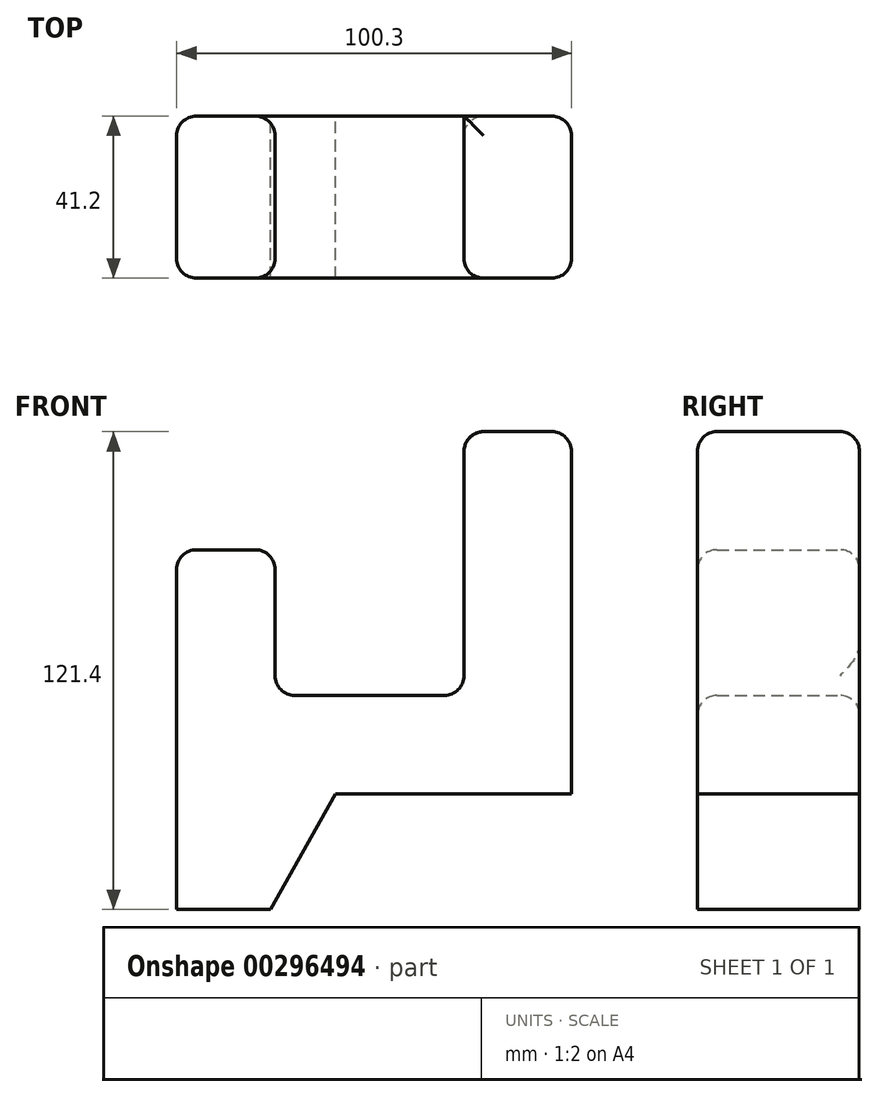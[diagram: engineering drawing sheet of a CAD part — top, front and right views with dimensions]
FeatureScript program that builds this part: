
annotation { "Feature Type Name" : "Feature", "Feature Type Description" : "" }
export const myFeature = defineFeature(function(context is Context, id is Id, definition is map)
    precondition{}
    {
        {
            var Q0;
            Q0=qCreatedBy(makeId("Front.planeOp"),FACE);
            var sketch = newSketch(context, id + "F0", { "sketchPlane" : qUnion([Q0])});
            skLineSegment(sketch, "E0", {"start": v(-107.75, 37) * mm, "end": v(-107.75, -54.4) * mm});
            skLineSegment(sketch, "E1", {"start": v(-107.75, 37) * mm, "end": v(-82.75, 37) * mm});
            skLineSegment(sketch, "E2", {"start": v(-82.75, 0) * mm, "end": v(-82.75, 37) * mm});
            skLineSegment(sketch, "E3", {"start": v(-82.75, 0) * mm, "end": v(-34.75, 0) * mm});
            skLineSegment(sketch, "E4", {"start": v(-34.75, 67) * mm, "end": v(-34.75, 0) * mm});
            skLineSegment(sketch, "E5", {"start": v(-34.75, 67) * mm, "end": v(-7.45, 67) * mm});
            skLineSegment(sketch, "E6", {"start": v(-7.45, 67) * mm, "end": v(-7.45, -25) * mm});
            skLineSegment(sketch, "E7", {"start": v(-7.45, -25) * mm, "end": v(-67.45, -25) * mm});
            skLineSegment(sketch, "E8", {"start": v(-107.75, -54.4) * mm, "end": v(-83.95, -54.4) * mm});
            skLineSegment(sketch, "E9", {"start": v(-67.45, -25) * mm, "end": v(-83.95, -54.4) * mm});
            skSolve(sketch);
        }
        {
            var Q0;
            Q0 = qSketchRegion(id + "F0", true);
            extrude(context, id + "F1", {"entities" : qUnion([Q0]), "endBound" : BoundingType.SYMMETRIC, "depth" : 41.2 * mm});
        }
        {
            var Q0;
            Q0=makeQuery(id+"F1.opExtrude","SWEPT_EDGE",EDGE,{"disambiguationData":[OSD([sQuery(id+"F0.wireOp",EDGE,"E0"),sQuery(id+"F0.wireOp",EDGE,"E1")])]});
            var Q1;
            Q1=makeQuery(id+"F1.opExtrude","SWEPT_EDGE",EDGE,{"disambiguationData":[OSD([sQuery(id+"F0.wireOp",EDGE,"E1"),sQuery(id+"F0.wireOp",EDGE,"E2")])]});
            var Q2;
            Q2=makeQuery(id+"F1.opExtrude","CAP_EDGE",EDGE,{"disambiguationData":[OSD([sQuery(id+"F0.wireOp",EDGE,"E1")])],"isStart":false});
            var Q3;
            Q3=makeQuery(id+"F1.opExtrude","CAP_EDGE",EDGE,{"disambiguationData":[OSD([sQuery(id+"F0.wireOp",EDGE,"E1")])],"isStart":true});
            var Q4;
            Q4=makeQuery(id+"F1.opExtrude","CAP_EDGE",EDGE,{"disambiguationData":[OSD([sQuery(id+"F0.wireOp",EDGE,"E2")])],"isStart":false});
            var Q5;
            Q5=makeQuery(id+"F1.opExtrude","SWEPT_EDGE",EDGE,{"disambiguationData":[OSD([sQuery(id+"F0.wireOp",EDGE,"E2"),sQuery(id+"F0.wireOp",EDGE,"E3")])]});
            var Q6;
            Q6=makeQuery(id+"F1.opExtrude","CAP_EDGE",EDGE,{"disambiguationData":[OSD([sQuery(id+"F0.wireOp",EDGE,"E2")])],"isStart":true});
            var Q7;
            Q7=makeQuery(id+"F1.opExtrude","CAP_EDGE",EDGE,{"disambiguationData":[OSD([sQuery(id+"F0.wireOp",EDGE,"E3")])],"isStart":true});
            var Q8;
            Q8=makeQuery(id+"F1.opExtrude","SWEPT_FACE",FACE,{"disambiguationData":[OSD([sQuery(id+"F0.wireOp",EDGE,"E3")])]});
            var Q9;
            Q9=makeQuery(id+"F1.opExtrude","CAP_EDGE",EDGE,{"disambiguationData":[OSD([sQuery(id+"F0.wireOp",EDGE,"E3")])],"isStart":false});
            var Q10;
            Q10=makeQuery(id+"F1.opExtrude","SWEPT_EDGE",EDGE,{"disambiguationData":[OSD([sQuery(id+"F0.wireOp",EDGE,"E4"),sQuery(id+"F0.wireOp",EDGE,"E5")])]});
            var Q11;
            Q11=makeQuery(id+"F1.opExtrude","CAP_EDGE",EDGE,{"disambiguationData":[OSD([sQuery(id+"F0.wireOp",EDGE,"E5")])],"isStart":false});
            var Q12;
            Q12=makeQuery(id+"F1.opExtrude","CAP_EDGE",EDGE,{"disambiguationData":[OSD([sQuery(id+"F0.wireOp",EDGE,"E5")])],"isStart":true});
            var Q13;
            Q13=makeQuery(id+"F1.opExtrude","SWEPT_EDGE",EDGE,{"disambiguationData":[OSD([sQuery(id+"F0.wireOp",EDGE,"E5"),sQuery(id+"F0.wireOp",EDGE,"E6")])]});
            var Q14;
            Q14=makeQuery(id+"F1.opExtrude","CAP_EDGE",EDGE,{"disambiguationData":[OSD([sQuery(id+"F0.wireOp",EDGE,"E4")])],"isStart":false});
            var Q15;
            Q15=makeQuery(id+"F1.opExtrude","CAP_EDGE",EDGE,{"disambiguationData":[OSD([sQuery(id+"F0.wireOp",EDGE,"E6")])],"isStart":false});
            var Q16;
            Q16=makeQuery(id+"F1.opExtrude","CAP_EDGE",EDGE,{"disambiguationData":[OSD([sQuery(id+"F0.wireOp",EDGE,"E6")])],"isStart":true});
            var Q17;
            Q17=makeQuery(id+"F1.opExtrude","CAP_EDGE",EDGE,{"disambiguationData":[OSD([sQuery(id+"F0.wireOp",EDGE,"E0")])],"isStart":false});
            var Q18;
            Q18=makeQuery(id+"F1.opExtrude","CAP_EDGE",EDGE,{"disambiguationData":[OSD([sQuery(id+"F0.wireOp",EDGE,"E0")])],"isStart":true});
            fillet(context, id + "F2", {"entities" : qUnion([Q0, Q1, Q2, Q3, Q4, Q5, Q6, Q7, Q8, Q9, Q10, Q11, Q12, Q13, Q14, Q15, Q16, Q17, Q18]), "radius" : 5 * mm, "tangentPropagation" : true, "allowEdgeOverflow" : false});
        }
    });
